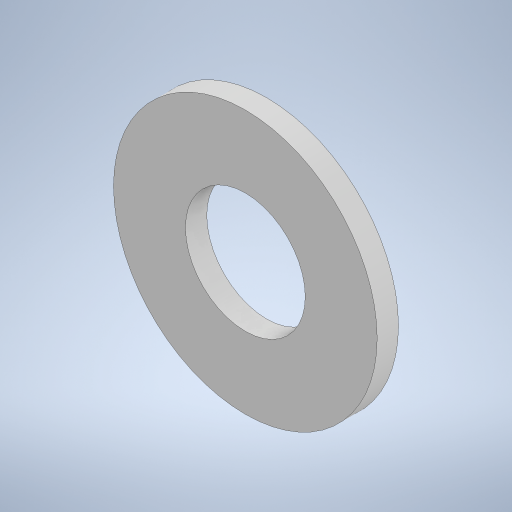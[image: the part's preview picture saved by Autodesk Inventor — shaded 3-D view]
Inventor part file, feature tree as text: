
AUTODESK INVENTOR PART (.ipt)
format: ipt  version: 2024 (Build 280153000, 153)  size: 219,136 bytes
history: native  units: in
note: dims shown in document units (in); Inventor stores cm internally (conversion verified against a paired STEP export)
features: extrude x1, sketch x1
ambient origin geometry x8: Origin, YZ Plane, XZ Plane, XY Plane, X Axis, Y Axis, Z Axis, Center Point
bodies: Solid1 (feature_tree)
feature tree (2):
  extrude  "Extrusion1"  Depth=0.04in
  sketch  "Sketch1"  dims[d0=0.135in d1=0.225in d2=0.04in d3=0.0in]
